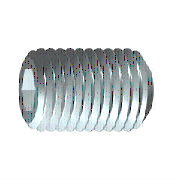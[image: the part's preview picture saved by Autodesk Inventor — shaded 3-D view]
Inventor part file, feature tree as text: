
AUTODESK INVENTOR PART (.ipt)
format: ipt  version: 2018 (Build 220112000, 112)  size: 176,640 bytes
history: native  units: mm (DEFAULTED — no unit token found)
features: sketch x2, extrude x1, other x1, plane x1
ambient origin geometry x8: Origin, YZ Plane, XZ Plane, XY Plane, X Axis, Y Axis, Z Axis, Center Point
bodies: Solid1 (feature_tree), Body (feature_tree)
feature tree (5):
  extrude  "Slot"  TaperAngle=60.0deg  [1 undecoded]
  other  "Work Axis1"
  plane  "Work Plane1"
  sketch  "Sketch1"  dims[d0=2.032mm d1=60.0deg]
  sketch  "Sketch2"  dims[d2=4.1656mm d3=2.287693mm d6=90.0deg d4=4.7625mm d5=10.297443mm d7=2.0828mm d8=2.032mm d9=0.0mm d10=1.0414mm d11=45.0deg d12=0.42926mm d13=45.0deg d14=4.7625mm d15=0.0mm d16=0.0mm d33=1.0414mm d34=0.42926mm d35=0.0mm d37=0.0mm]
note: 1 required parameter value undecoded (feature->parameter linkage not recoverable at this tier; creation-order binding heuristic only, values carry confidence <= 0.55)
